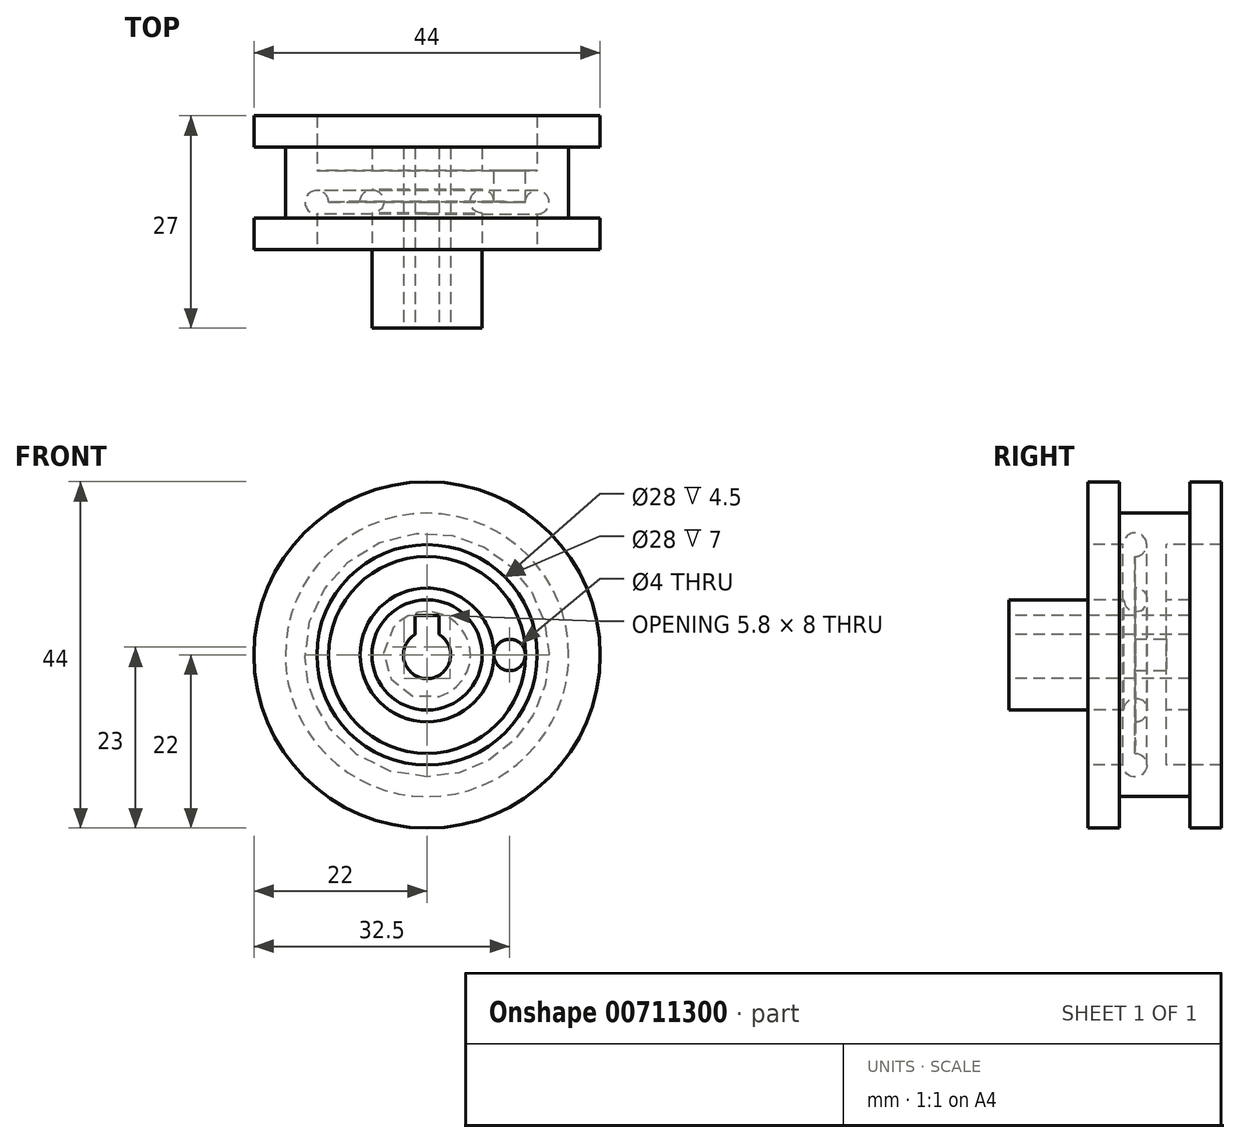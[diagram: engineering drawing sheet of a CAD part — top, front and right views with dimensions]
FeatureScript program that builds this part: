
annotation { "Feature Type Name" : "Feature", "Feature Type Description" : "" }
export const myFeature = defineFeature(function(context is Context, id is Id, definition is map)
    precondition{}
    {
        {
            var Q0;
            Q0=qCreatedBy(makeId("Right.planeOp"),FACE);
            var sketch = newSketch(context, id + "F0", { "sketchPlane" : qUnion([Q0])});
            skLineSegment(sketch, "E0", {"start": v(-16.34, 0) * mm, "end": v(15.32, 0) * mm, "construction": true});
            skLineSegment(sketch, "E1", {"start": v(4.5, -7) * mm, "end": v(-11.6, -7) * mm});
            skLineSegment(sketch, "E2", {"start": v(-11.6, -7) * mm, "end": v(-11.6, -3) * mm});
            skLineSegment(sketch, "E3", {"start": v(-11.6, -3) * mm, "end": v(11.4, -3) * mm});
            skLineSegment(sketch, "E4", {"start": v(11.4, -3) * mm, "end": v(11.4, -7) * mm});
            skLineSegment(sketch, "E5", {"start": v(11.4, -7) * mm, "end": v(8.4, -7) * mm});
            skLineSegment(sketch, "E6", {"start": v(8.4, -7) * mm, "end": v(8.4, -14) * mm});
            skLineSegment(sketch, "E7", {"start": v(8.4, -14) * mm, "end": v(15.4, -14) * mm});
            skLineSegment(sketch, "E8", {"start": v(15.4, -14) * mm, "end": v(15.4, -22) * mm});
            skLineSegment(sketch, "E9", {"start": v(15.4, -22) * mm, "end": v(11.4, -22) * mm});
            skLineSegment(sketch, "E10", {"start": v(11.4, -22) * mm, "end": v(11.4, -18) * mm});
            skLineSegment(sketch, "E11", {"start": v(11.4, -18) * mm, "end": v(2.4, -18) * mm});
            skLineSegment(sketch, "E12", {"start": v(2.4, -18) * mm, "end": v(2.4, -22) * mm});
            skLineSegment(sketch, "E13", {"start": v(2.4, -22) * mm, "end": v(-1.6, -22) * mm});
            skLineSegment(sketch, "E14", {"start": v(-1.6, -22) * mm, "end": v(-1.6, -14) * mm});
            skLineSegment(sketch, "E15", {"start": v(-1.6, -14) * mm, "end": v(4.4, -14) * mm});
            skLineSegment(sketch, "E16", {"start": v(4.4, -14) * mm, "end": v(4.5, -7) * mm});
            skSolve(sketch);
        }
        {
            var Q0;
            Q0=makeQuery(id+"F0.imprint","IMPRINT",FACE,{"disambiguationData":[TD([[makeQuery(id+"F0.imprint","IMPRINT",EDGE,{"derivedFrom":sQuery(id+"F0.wireOp",EDGE,"E1")}),-1.0]])]});
            var Q1;
            Q1=sQuery(id+"F0.wireOp",EDGE,"E0");
            revolve(context, id + "F1", {"surfaceOperationType" : NewSurfaceOperationType.NEW, "entities" : qUnion([Q0]), "axis" : qUnion([Q1]), "revolveType" : RevolveType.FULL});
        }
        {
            var Q0;
            Q0=makeQuery(id+"F1.opRevolve","SWEPT_FACE",FACE,{"disambiguationData":[OSD([sQuery(id+"F0.wireOp",EDGE,"E2")])]});
            var sketch = newSketch(context, id + "F2", { "sketchPlane" : qUnion([Q0])});
            skLineSegment(sketch, "E17.bottom", {"start": v(-1.5, 0) * mm, "end": v(1.5, 0) * mm});
            skLineSegment(sketch, "E17.top", {"start": v(-1.5, 5) * mm, "end": v(1.5, 5) * mm});
            skLineSegment(sketch, "E17.left", {"start": v(-1.5, 0) * mm, "end": v(-1.5, 5) * mm});
            skLineSegment(sketch, "E17.right", {"start": v(1.5, 0) * mm, "end": v(1.5, 5) * mm});
            skSolve(sketch);
        }
        {
            var Q0;
            {var subQ0=sQuery(id+"F2.wireOp",EDGE,"E17.top");Q0=makeQuery(id+"F2.imprint","IMPRINT",FACE,{"disambiguationData":[TD([[makeQuery(id+"F2.imprint","IMPRINT",EDGE,{"derivedFrom":subQ0}),-1.0]])]});}
            var Q1;
            {var subQ0=sQuery(id+"F2.wireOp",EDGE,"E17.bottom");Q1=makeQuery(id+"F2.imprint","IMPRINT",FACE,{"disambiguationData":[TD([[makeQuery(id+"F2.imprint","IMPRINT",EDGE,{"derivedFrom":subQ0}),1.0]])]});}
            extrude(context, id + "F3", {"entities" : qUnion([Q0, Q1]), "operationType" : NewBodyOperationType.REMOVE, "endBound" : BoundingType.THROUGH_ALL, "oppositeDirection" : true, "depth" : 25 * mm, "offsetDistance" : 25 * mm});
        }
        {
            var Q0;
            Q0=makeQuery(id+"F1.opRevolve","SWEPT_FACE",FACE,{"disambiguationData":[OSD([sQuery(id+"F0.wireOp",EDGE,"E6")])]});
            var sketch = newSketch(context, id + "F4", { "sketchPlane" : qUnion([Q0])});
            skCircle(sketch, "E18", {"center": v(-10.5, 0) * mm, "radius": 2 * mm});
            skSolve(sketch);
        }
        {
            var Q0;
            Q0=makeQuery(id+"F4.imprint","IMPRINT",FACE,{"disambiguationData":[TD([[makeQuery(id+"F4.imprint","IMPRINT",EDGE,{"derivedFrom":sQuery(id+"F4.wireOp",EDGE,"E18")}),1.0]])]});
            extrude(context, id + "F5", {"entities" : qUnion([Q0]), "operationType" : NewBodyOperationType.REMOVE, "endBound" : BoundingType.THROUGH_ALL, "oppositeDirection" : true, "depth" : 25 * mm, "offsetDistance" : 25 * mm});
        }
        {
            var Q0;
            Q0=qCreatedBy(makeId("Top.planeOp"),FACE);
            var sketch = newSketch(context, id + "F6", { "sketchPlane" : qUnion([Q0])});
            skCircle(sketch, "E19", {"center": v(14, 4.4) * mm, "radius": 1.5 * mm});
            skCircle(sketch, "E20", {"center": v(7, 4.5) * mm, "radius": 1.5 * mm});
            skSolve(sketch);
        }
        {
            var Q0;
            Q0=makeQuery(id+"F6.imprint","IMPRINT",FACE,{"disambiguationData":[TD([[makeQuery(id+"F6.imprint","IMPRINT",EDGE,{"derivedFrom":sQuery(id+"F6.wireOp",EDGE,"E19")}),1.0]])]});
            var Q1;
            Q1=makeQuery(id+"F6.imprint","IMPRINT",FACE,{"disambiguationData":[TD([[makeQuery(id+"F6.imprint","IMPRINT",EDGE,{"derivedFrom":sQuery(id+"F6.wireOp",EDGE,"E20")}),1.0]])]});
            var Q2;
            Q2=makeQuery(id+"F1.opRevolve","SWEPT_EDGE",EDGE,{"disambiguationData":[OSD([sQuery(id+"F0.wireOp",EDGE,"E15"),sQuery(id+"F0.wireOp",EDGE,"E16")])]});
            sweep(context, id + "F7", {"operationType" : NewBodyOperationType.REMOVE, "profiles" : qUnion([Q0, Q1]), "path" : qUnion([Q2])});
        }
    });
